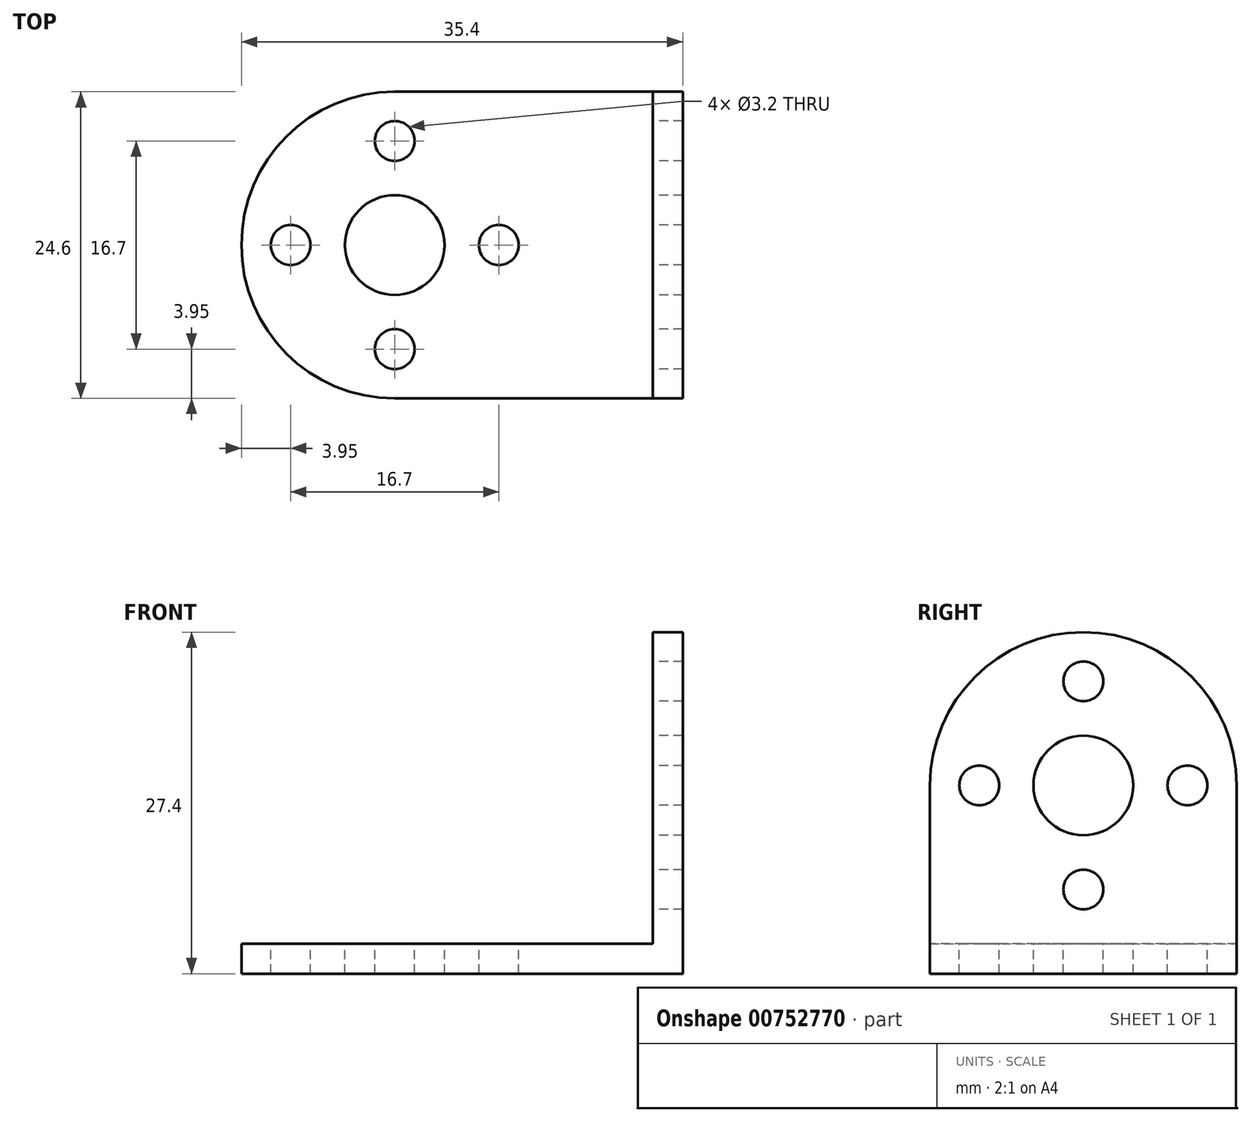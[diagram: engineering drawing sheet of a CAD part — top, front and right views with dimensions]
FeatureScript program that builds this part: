
annotation { "Feature Type Name" : "Feature", "Feature Type Description" : "" }
export const myFeature = defineFeature(function(context is Context, id is Id, definition is map)
    precondition{}
    {
        {
            var Q0;
            Q0=qCreatedBy(makeId("Top.planeOp"),FACE);
            var sketch = newSketch(context, id + "F0", { "sketchPlane" : qUnion([Q0])});
            skLineSegment(sketch, "E0.bottom", {"start": v(17.7, -12.3) * mm, "end": v(-17.7, -12.3) * mm});
            skLineSegment(sketch, "E0.top", {"start": v(17.7, 12.3) * mm, "end": v(-17.7, 12.3) * mm});
            skLineSegment(sketch, "E0.left", {"start": v(17.7, -12.3) * mm, "end": v(17.7, 12.3) * mm});
            skLineSegment(sketch, "E0.right", {"start": v(-17.7, -12.3) * mm, "end": v(-17.7, 12.3) * mm});
            skPoint(sketch, "E0.middle", {"position": v(0, 0) * mm});
            skSolve(sketch);
        }
        {
            var Q0;
            Q0 = qSketchRegion(id + "F0", true);
            extrude(context, id + "F1", {"entities" : qUnion([Q0]), "depth" : 2.4 * mm, "offsetDistance" : 25 * mm});
        }
        {
            var Q0;
            Q0=makeQuery(id+"F1.opExtrude","CAP_FACE",FACE,{"disambiguationData":[OSD([sQuery(id+"F0.wireOp",EDGE,"E0.bottom"),sQuery(id+"F0.wireOp",EDGE,"E0.top"),sQuery(id+"F0.wireOp",EDGE,"E0.left"),sQuery(id+"F0.wireOp",EDGE,"E0.right")])],"isStart":false});
            var sketch = newSketch(context, id + "F2", { "sketchPlane" : qUnion([Q0])});
            skLineSegment(sketch, "E1.bottom", {"start": v(17.7, -12.3) * mm, "end": v(15.3, -12.3) * mm});
            skLineSegment(sketch, "E1.top", {"start": v(17.7, 12.3) * mm, "end": v(15.3, 12.3) * mm});
            skLineSegment(sketch, "E1.left", {"start": v(17.7, -12.3) * mm, "end": v(17.7, 12.3) * mm});
            skLineSegment(sketch, "E1.right", {"start": v(15.3, -12.3) * mm, "end": v(15.3, 12.3) * mm});
            skSolve(sketch);
        }
        {
            var Q0;
            Q0 = qSketchRegion(id + "F2", true);
            extrude(context, id + "F3", {"entities" : qUnion([Q0]), "operationType" : NewBodyOperationType.ADD, "depth" : 25 * mm, "offsetDistance" : 25 * mm});
        }
        {
            var Q0;
            Q0=makeQuery(id+"F3.opExtrude","CAP_EDGE",EDGE,{"disambiguationData":[OSD([sQuery(id+"F2.wireOp",EDGE,"E1.bottom")])],"isStart":false});
            var Q1;
            Q1=makeQuery(id+"F3.opExtrude","CAP_EDGE",EDGE,{"disambiguationData":[OSD([sQuery(id+"F2.wireOp",EDGE,"E1.top")])],"isStart":false});
            var Q2;
            Q2=makeQuery(id+"F1.opExtrude","SWEPT_EDGE",EDGE,{"disambiguationData":[OSD([sQuery(id+"F0.wireOp",EDGE,"E0.bottom"),sQuery(id+"F0.wireOp",EDGE,"E0.right")])]});
            var Q3;
            Q3=makeQuery(id+"F1.opExtrude","SWEPT_EDGE",EDGE,{"disambiguationData":[OSD([sQuery(id+"F0.wireOp",EDGE,"E0.top"),sQuery(id+"F0.wireOp",EDGE,"E0.right")])]});
            fillet(context, id + "F4", {"entities" : qUnion([Q0, Q1, Q2, Q3]), "radius" : 12.3 * mm, "tangentPropagation" : true, "allowEdgeOverflow" : false});
        }
        {
            var Q0;
            Q0=makeQuery(id+"F3.opExtrude","SWEPT_FACE",FACE,{"disambiguationData":[OSD([sQuery(id+"F2.wireOp",EDGE,"E1.right")])]});
            var sketch = newSketch(context, id + "F5", { "sketchPlane" : qUnion([Q0])});
            skCircle(sketch, "E2", {"center": v(0, 15.1) * mm, "radius": 4 * mm});
            skLineSegment(sketch, "E3", {"start": v(0, 15.1) * mm, "end": v(0, 23.45) * mm});
            skCircle(sketch, "E4", {"center": v(0, 23.45) * mm, "radius": 1.6 * mm});
            skCircle(sketch, "E5.1.0", {"center": v(-8.35, 15.1) * mm, "radius": 1.6 * mm});
            skCircle(sketch, "E5.2.0", {"center": v(0, 6.75) * mm, "radius": 1.6 * mm});
            skCircle(sketch, "E5.3.0", {"center": v(8.35, 15.1) * mm, "radius": 1.6 * mm});
            skSolve(sketch);
        }
        {
            var Q0;
            Q0 = qSketchRegion(id + "F5", true);
            extrude(context, id + "F6", {"entities" : qUnion([Q0]), "operationType" : NewBodyOperationType.REMOVE, "oppositeDirection" : true, "depth" : 3 * mm, "offsetDistance" : 25 * mm});
        }
        {
            var Q0;
            Q0=makeQuery(id+"F1.opExtrude","CAP_FACE",FACE,{"disambiguationData":[OSD([sQuery(id+"F0.wireOp",EDGE,"E0.bottom"),sQuery(id+"F0.wireOp",EDGE,"E0.top"),sQuery(id+"F0.wireOp",EDGE,"E0.left"),sQuery(id+"F0.wireOp",EDGE,"E0.right")])],"isStart":false});
            var sketch = newSketch(context, id + "F7", { "sketchPlane" : qUnion([Q0])});
            skCircle(sketch, "E6", {"center": v(-5.4, 0) * mm, "radius": 4 * mm});
            skLineSegment(sketch, "E7", {"start": v(-5.4, 0) * mm, "end": v(-13.75, 0) * mm});
            skCircle(sketch, "E8", {"center": v(-13.75, 0) * mm, "radius": 1.6 * mm});
            skCircle(sketch, "E9.1.0", {"center": v(-5.4, -8.35) * mm, "radius": 1.6 * mm});
            skCircle(sketch, "E9.2.0", {"center": v(2.95, 0) * mm, "radius": 1.6 * mm});
            skCircle(sketch, "E9.3.0", {"center": v(-5.4, 8.35) * mm, "radius": 1.6 * mm});
            skSolve(sketch);
        }
        {
            var Q0;
            Q0 = qSketchRegion(id + "F7", true);
            extrude(context, id + "F8", {"entities" : qUnion([Q0]), "operationType" : NewBodyOperationType.REMOVE, "oppositeDirection" : true, "depth" : 3 * mm, "offsetDistance" : 25 * mm});
        }
    });
